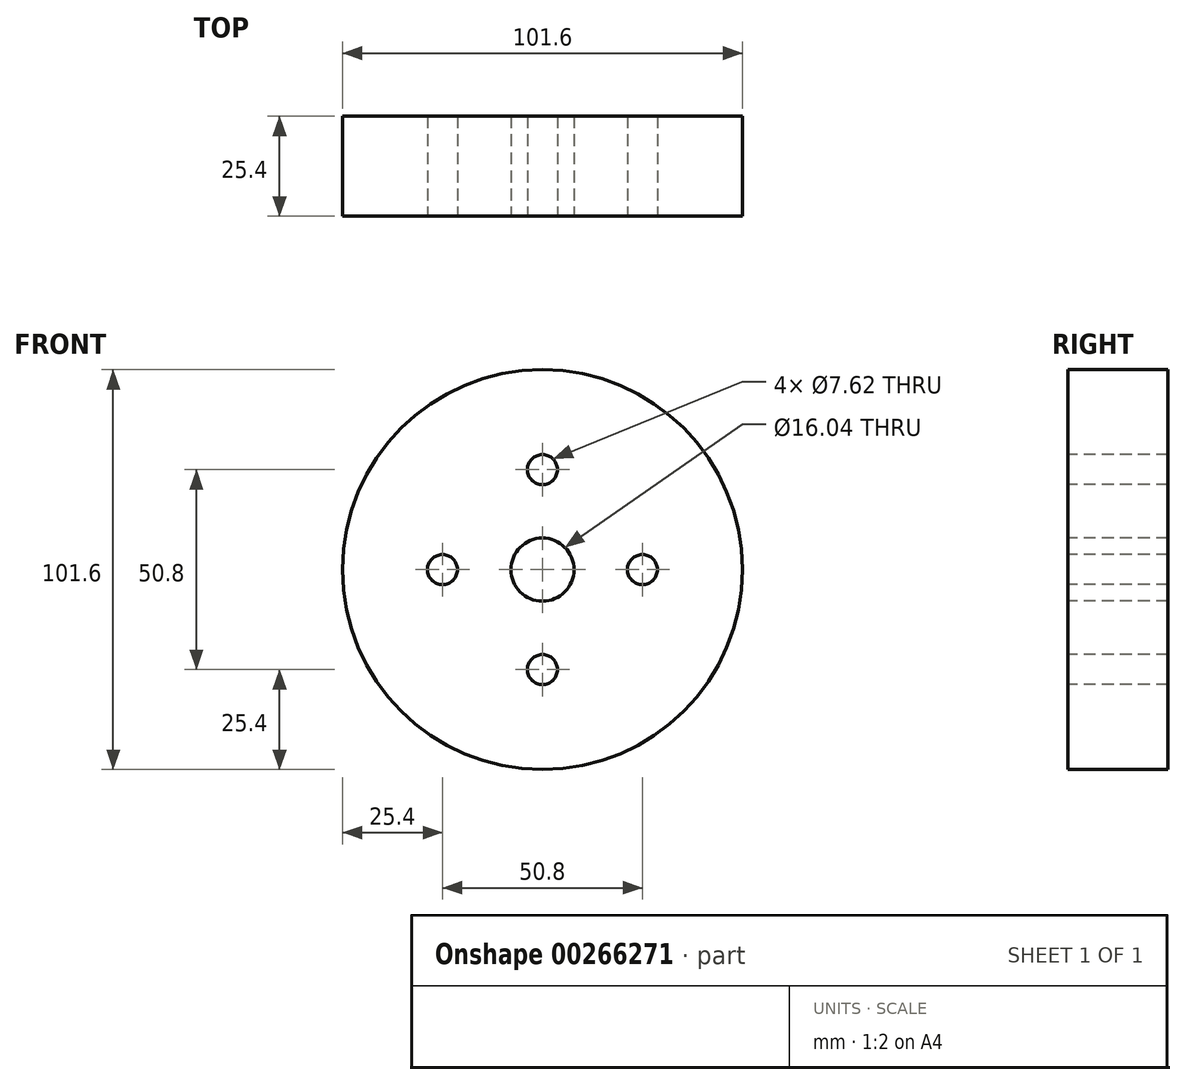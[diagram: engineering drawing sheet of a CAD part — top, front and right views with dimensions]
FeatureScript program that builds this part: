
annotation { "Feature Type Name" : "Feature", "Feature Type Description" : "" }
export const myFeature = defineFeature(function(context is Context, id is Id, definition is map)
    precondition{}
    {
        {
            var Q0;
            Q0=qCreatedBy(makeId("Front.planeOp"),FACE);
            var sketch = newSketch(context, id + "F0", { "sketchPlane" : qUnion([Q0])});
            skCircle(sketch, "E0", {"center": v(0, 0) * mm, "radius": 50.8 * mm});
            skSolve(sketch);
        }
        {
            var Q0;
            Q0 = qSketchRegion(id + "F0", true);
            extrude(context, id + "F1", {"entities" : qUnion([Q0]), "depth" : 25.4 * mm});
        }
        {
            var Q0;
            Q0=makeQuery(id+"F1.opExtrude","CAP_FACE",FACE,{"disambiguationData":[OSD([sQuery(id+"F0.wireOp",EDGE,"E0")])],"isStart":false});
            var sketch = newSketch(context, id + "F2", { "sketchPlane" : qUnion([Q0])});
            skCircle(sketch, "E1", {"center": v(0, 0) * mm, "radius": 8.02 * mm});
            skSolve(sketch);
        }
        {
            var Q0;
            Q0 = qSketchRegion(id + "F2", true);
            extrude(context, id + "F3", {"entities" : qUnion([Q0]), "operationType" : NewBodyOperationType.REMOVE, "oppositeDirection" : true, "depth" : 88.4 * mm});
        }
        {
            var Q0;
            Q0=makeQuery(id+"F1.opExtrude","CAP_FACE",FACE,{"disambiguationData":[OSD([sQuery(id+"F0.wireOp",EDGE,"E0")])],"isStart":false});
            var sketch = newSketch(context, id + "F4", { "sketchPlane" : qUnion([Q0])});
            skCircle(sketch, "E2", {"center": v(0, -25.4) * mm, "radius": 3.81 * mm});
            skCircle(sketch, "E3", {"center": v(-25.4, 0) * mm, "radius": 3.81 * mm});
            skCircle(sketch, "E4", {"center": v(25.4, 0) * mm, "radius": 3.81 * mm});
            skCircle(sketch, "E5", {"center": v(0, 25.4) * mm, "radius": 3.81 * mm});
            skSolve(sketch);
        }
        {
            var Q0;
            Q0=makeQuery(id+"F4.imprint","IMPRINT",FACE,{"disambiguationData":[TD([[makeQuery(id+"F4.imprint","IMPRINT",EDGE,{"derivedFrom":sQuery(id+"F4.wireOp",EDGE,"E2")}),-1.0]])]});
            var sketch = newSketch(context, id + "F5", { "sketchPlane" : qUnion([Q0])});
            skSolve(sketch);
        }
        {
            var Q0;
            Q0 = qSketchRegion(id + "F5", true);
            var Q1;
            Q1=makeQuery(id+"F4.imprint","IMPRINT",FACE,{"disambiguationData":[TD([[makeQuery(id+"F4.imprint","IMPRINT",EDGE,{"derivedFrom":sQuery(id+"F4.wireOp",EDGE,"E5")}),1.0]])]});
            var Q2;
            Q2=makeQuery(id+"F4.imprint","IMPRINT",FACE,{"disambiguationData":[TD([[makeQuery(id+"F4.imprint","IMPRINT",EDGE,{"derivedFrom":sQuery(id+"F4.wireOp",EDGE,"E3")}),1.0]])]});
            var Q3;
            Q3=makeQuery(id+"F4.imprint","IMPRINT",FACE,{"disambiguationData":[TD([[makeQuery(id+"F4.imprint","IMPRINT",EDGE,{"derivedFrom":sQuery(id+"F4.wireOp",EDGE,"E2")}),1.0]])]});
            var Q4;
            Q4=makeQuery(id+"F4.imprint","IMPRINT",FACE,{"disambiguationData":[TD([[makeQuery(id+"F4.imprint","IMPRINT",EDGE,{"derivedFrom":sQuery(id+"F4.wireOp",EDGE,"E4")}),1.0]])]});
            extrude(context, id + "F6", {"entities" : qUnion([Q0, Q1, Q2, Q3, Q4]), "operationType" : NewBodyOperationType.REMOVE, "oppositeDirection" : true, "depth" : 25.4 * mm});
        }
    });
